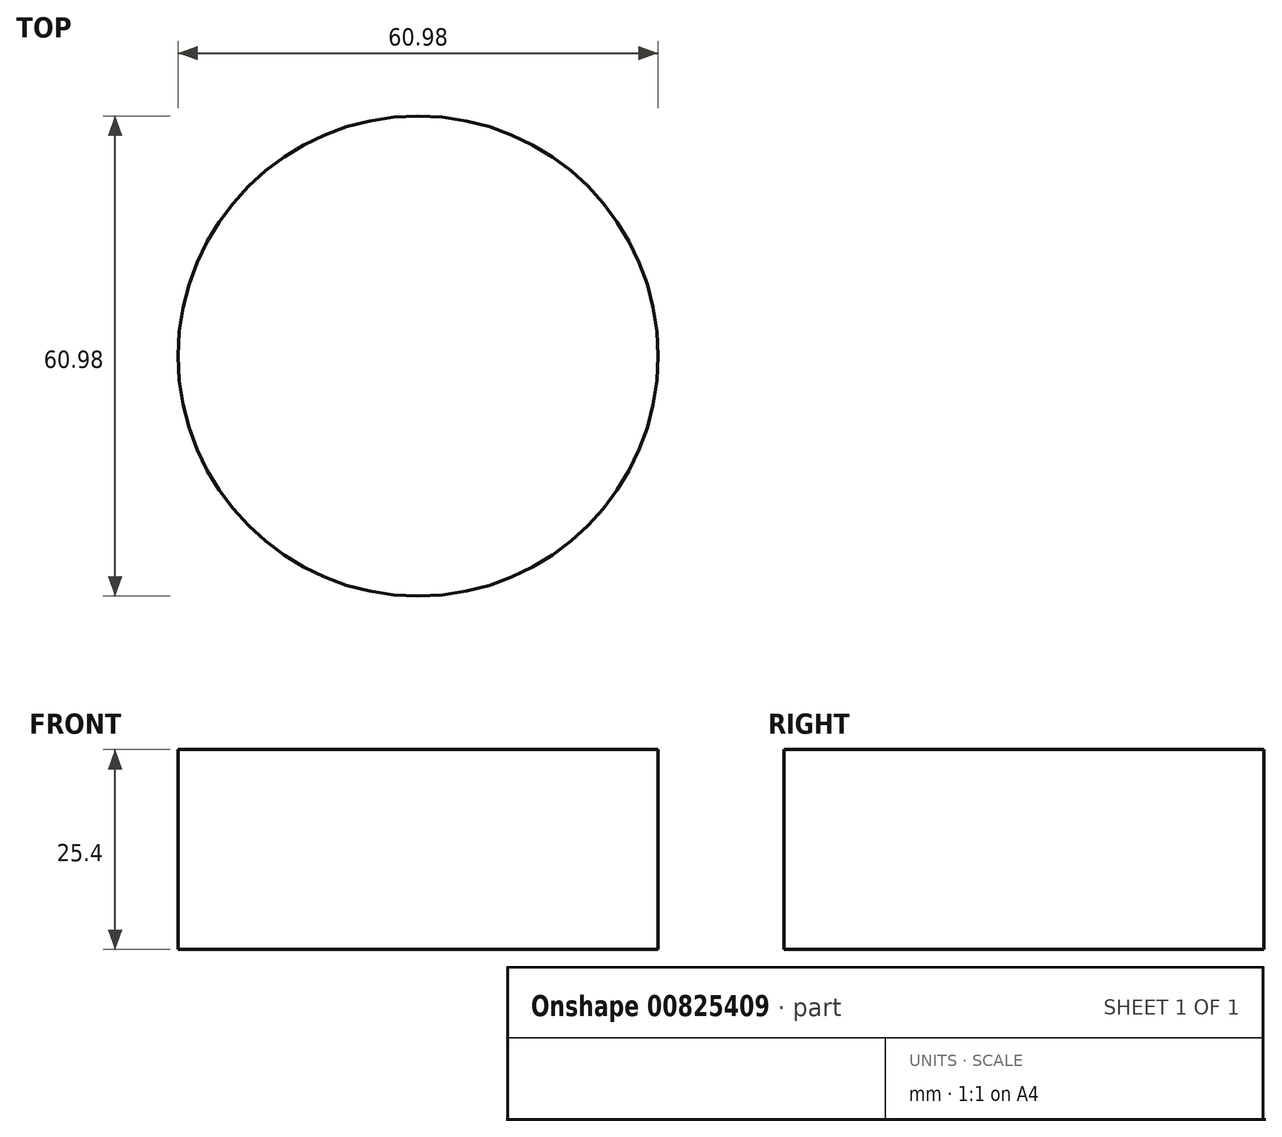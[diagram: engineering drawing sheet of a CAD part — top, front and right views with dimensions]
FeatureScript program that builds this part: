
annotation { "Feature Type Name" : "Feature", "Feature Type Description" : "" }
export const myFeature = defineFeature(function(context is Context, id is Id, definition is map)
    precondition{}
    {
        {
            var Q0;
            Q0=qCreatedBy(makeId("Top.planeOp"),FACE);
            var sketch = newSketch(context, id + "F0", { "sketchPlane" : qUnion([Q0])});
            skCircle(sketch, "E0", {"center": v(0, 0) * mm, "radius": 30.49 * mm});
            skSolve(sketch);
        }
        {
            var Q0;
            Q0 = qSketchRegion(id + "F0", true);
            extrude(context, id + "F1", {"entities" : qUnion([Q0]), "depth" : 25.4 * mm, "offsetDistance" : 25.4 * mm});
        }
    });
